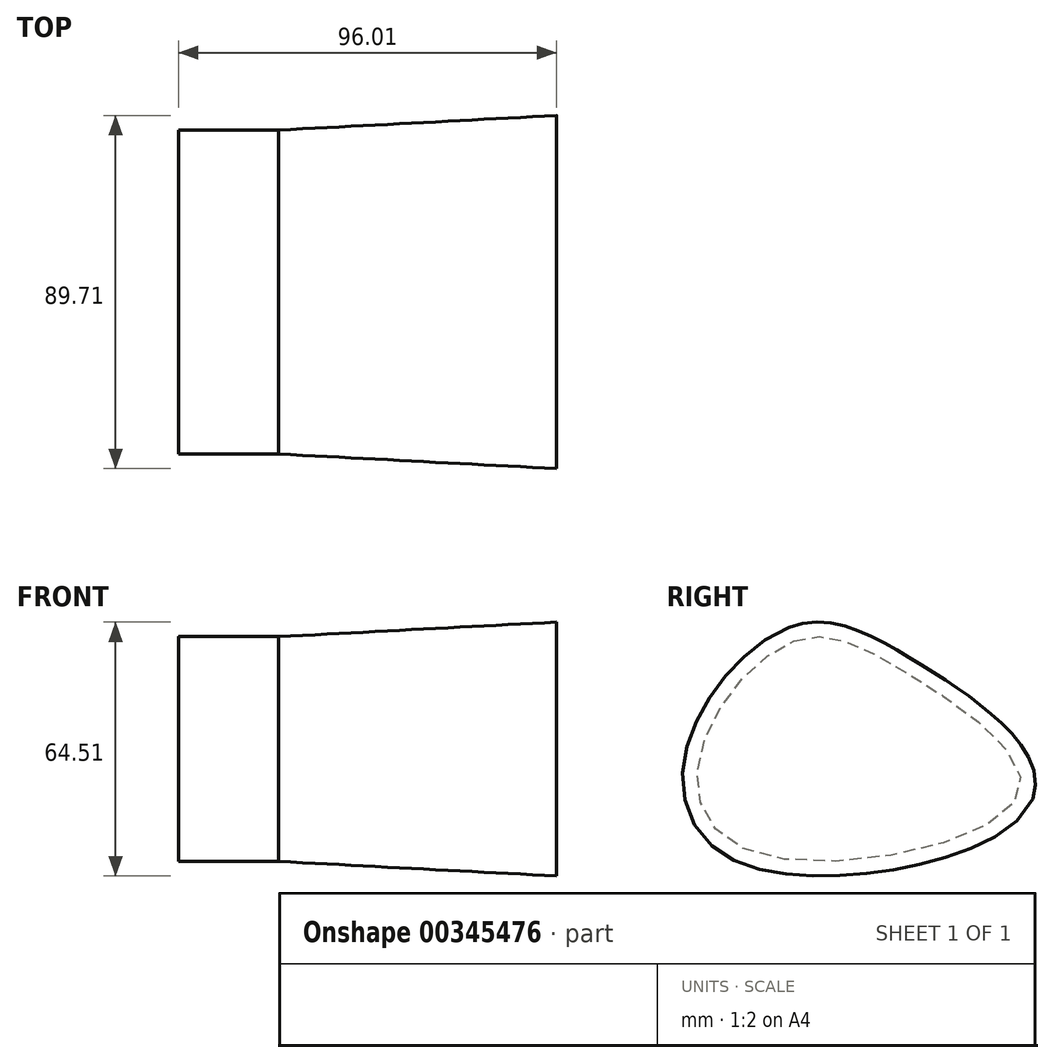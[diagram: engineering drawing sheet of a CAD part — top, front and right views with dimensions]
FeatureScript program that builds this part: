
annotation { "Feature Type Name" : "Feature", "Feature Type Description" : "" }
export const myFeature = defineFeature(function(context is Context, id is Id, definition is map)
    precondition{}
    {
        {
            var Q0;
            Q0=qCreatedBy(makeId("Right.planeOp"),FACE);
            var sketch = newSketch(context, id + "F0", { "sketchPlane" : qUnion([Q0])});
            skFitSpline(sketch, "E0", {"points": [v(-35.97, 48) * mm, v(-59.76, 19.4) * mm, v(-45.88, -5.8) * mm, v(21.24, 9.2) * mm, v(-8.5, 40.64) * mm, v(-35.97, 48) * mm]});
            skSolve(sketch);
        }
        {
            var Q0;
            Q0=makeQuery(id+"F0.imprint","IMPRINT",FACE,{"disambiguationData":[TD([[makeQuery(id+"F0.imprint","IMPRINT",EDGE,{"derivedFrom":sQuery(id+"F0.wireOp",EDGE,"E0")}),1.0]])]});
            var Q1;
            Q1=sQuery(id+"F0.wireOp",EDGE,"E0");
            extrude(context, id + "F1", {"entities" : qUnion([Q0]), "surfaceEntities" : qUnion([Q1]), "depth" : 70.61 * mm, "hasDraft" : true, "draftAngle" : 3 * degree, "hasSecondDirection" : true, "secondDirectionOppositeDirection" : true, "secondDirectionDepth" : 25.4 * mm});
        }
    });
